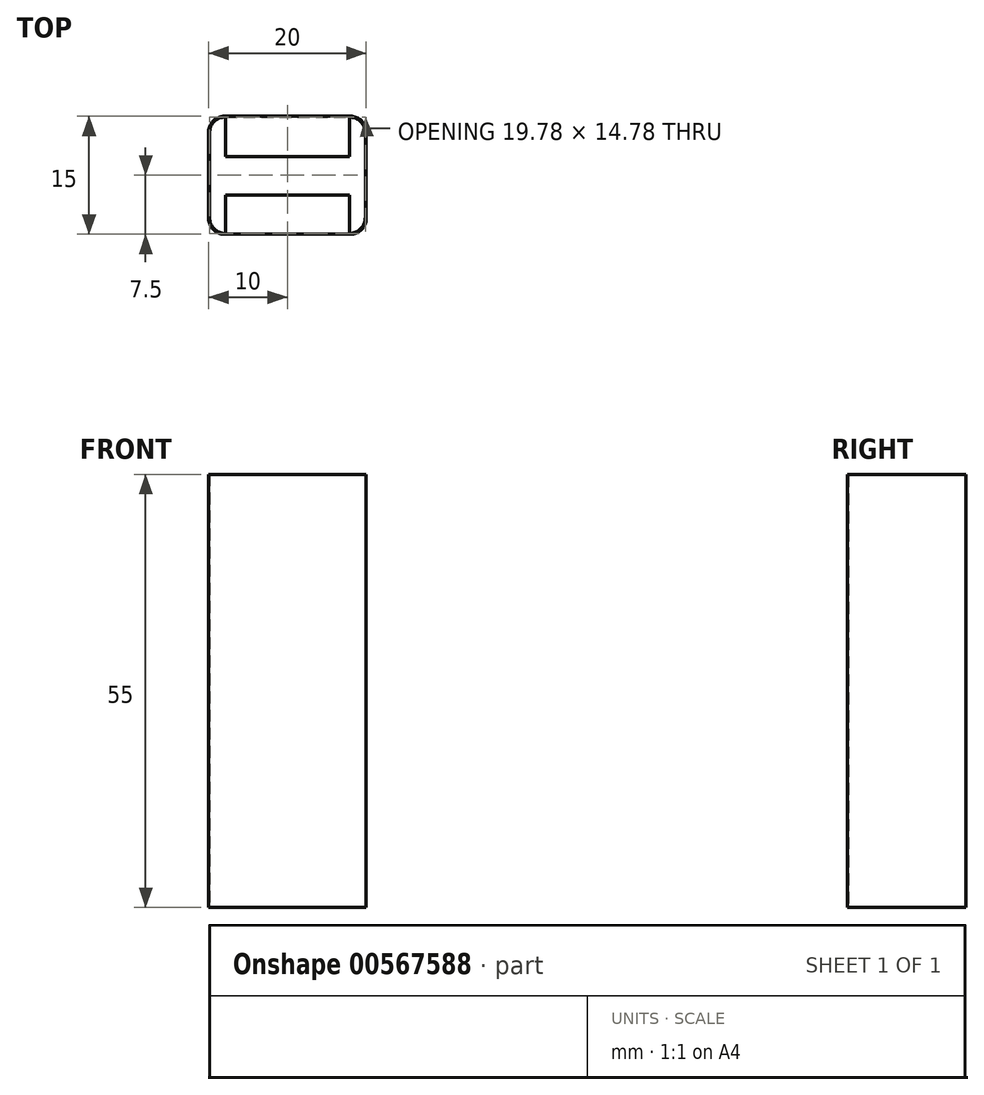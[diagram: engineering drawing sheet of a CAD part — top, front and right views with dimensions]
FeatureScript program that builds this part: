
annotation { "Feature Type Name" : "Feature", "Feature Type Description" : "" }
export const myFeature = defineFeature(function(context is Context, id is Id, definition is map)
    precondition{}
    {
        {
            var Q0;
            Q0=qCreatedBy(makeId("Top.planeOp"),FACE);
            var sketch = newSketch(context, id + "F0", { "sketchPlane" : qUnion([Q0])});
            skLineSegment(sketch, "E0.bottom", {"start": v(8, -7.5) * mm, "end": v(-8, -7.5) * mm});
            skLineSegment(sketch, "E0.top", {"start": v(8, 7.5) * mm, "end": v(-8, 7.5) * mm});
            skLineSegment(sketch, "E0.left", {"start": v(10, -5.5) * mm, "end": v(10, 5.5) * mm});
            skLineSegment(sketch, "E0.right", {"start": v(-10, -5.5) * mm, "end": v(-10, 5.5) * mm});
            skPoint(sketch, "E0.middle", {"position": v(0, 0) * mm});
            skPoint(sketch, "E1.visualSharp", {"position": v(-10, 7.5) * mm});
            skArc(sketch, "E1.filletArc", {"start": v(-8, 7.5) * mm, "mid": v(-9.41, 6.91) * mm, "end": v(-10, 5.5) * mm});
            skPoint(sketch, "E2.visualSharp", {"position": v(10, 7.5) * mm});
            skArc(sketch, "E2.filletArc", {"start": v(10, 5.5) * mm, "mid": v(9.41, 6.91) * mm, "end": v(8, 7.5) * mm});
            skPoint(sketch, "E3.visualSharp", {"position": v(10, -7.5) * mm});
            skArc(sketch, "E3.filletArc", {"start": v(8, -7.5) * mm, "mid": v(9.41, -6.91) * mm, "end": v(10, -5.5) * mm});
            skPoint(sketch, "E4.visualSharp", {"position": v(-10, -7.5) * mm});
            skArc(sketch, "E4.filletArc", {"start": v(-10, -5.5) * mm, "mid": v(-9.41, -6.91) * mm, "end": v(-8, -7.5) * mm});
            skLineSegment(sketch, "E5.0", {"start": v(7.9, 7.4) * mm, "end": v(-7.9, 7.39) * mm});
            skLineSegment(sketch, "E5.1", {"start": v(9.9, -5.4) * mm, "end": v(9.9, 5.4) * mm});
            skLineSegment(sketch, "E5.2", {"start": v(7.9, -7.39) * mm, "end": v(-7.89, -7.4) * mm});
            skLineSegment(sketch, "E5.3", {"start": v(-9.89, -5.4) * mm, "end": v(-9.89, 5.39) * mm});
            skPoint(sketch, "E6.visualSharp", {"position": v(-9.9, 7.39) * mm});
            skArc(sketch, "E6.filletArc", {"start": v(-7.9, 7.39) * mm, "mid": v(-9.3, 6.8) * mm, "end": v(-9.89, 5.39) * mm});
            skPoint(sketch, "E7.visualSharp", {"position": v(-9.89, -7.4) * mm});
            skArc(sketch, "E7.filletArc", {"start": v(-9.89, -5.4) * mm, "mid": v(-9.3, -6.8) * mm, "end": v(-7.89, -7.39) * mm});
            skPoint(sketch, "E8.visualSharp", {"position": v(9.9, -7.39) * mm});
            skArc(sketch, "E8.filletArc", {"start": v(7.9, -7.39) * mm, "mid": v(9.3, -6.8) * mm, "end": v(9.9, -5.4) * mm});
            skPoint(sketch, "E9.visualSharp", {"position": v(9.89, 7.4) * mm});
            skArc(sketch, "E9.filletArc", {"start": v(9.89, 5.4) * mm, "mid": v(9.3, 6.8) * mm, "end": v(7.9, 7.4) * mm});
            skSolve(sketch);
        }
        {
            var Q0;
            Q0=makeQuery(id+"F0.imprint","IMPRINT",FACE,{"disambiguationData":[TD([[makeQuery(id+"F0.imprint","IMPRINT",EDGE,{"derivedFrom":sQuery(id+"F0.wireOp",EDGE,"E0.bottom")}),-1.0]])]});
            extrude(context, id + "F1", {"entities" : qUnion([Q0]), "depth" : 30 * mm, "offsetDistance" : 25 * mm});
        }
        {
            var Q0;
            Q0=makeQuery(id+"F1.opExtrude","SWEPT_FACE",FACE,{"disambiguationData":[OSD([sQuery(id+"F0.wireOp",EDGE,"E5.0")])]});
            var sketch = newSketch(context, id + "F2", { "sketchPlane" : qUnion([Q0])});
            skLineSegment(sketch, "E10.bottom", {"start": v(-7.89, 30) * mm, "end": v(7.9, 30) * mm});
            skLineSegment(sketch, "E10.top", {"start": v(-7.89, 29.89) * mm, "end": v(7.9, 29.89) * mm});
            skLineSegment(sketch, "E10.left", {"start": v(-7.89, 30) * mm, "end": v(-7.89, 29.89) * mm});
            skLineSegment(sketch, "E10.right", {"start": v(7.9, 30) * mm, "end": v(7.9, 29.89) * mm});
            skSolve(sketch);
        }
        {
            var Q0;
            Q0=makeQuery(id+"F2.imprint","IMPRINT",FACE,{"disambiguationData":[TD([[makeQuery(id+"F2.imprint","IMPRINT",EDGE,{"derivedFrom":sQuery(id+"F2.wireOp",EDGE,"E10.bottom")}),1.0]])]});
            extrude(context, id + "F3", {"entities" : qUnion([Q0]), "operationType" : NewBodyOperationType.ADD, "depth" : 5 * mm, "offsetDistance" : 25 * mm});
        }
        {
            var Q0;
            Q0=makeQuery(id+"F1.opExtrude","SWEPT_FACE",FACE,{"disambiguationData":[OSD([sQuery(id+"F0.wireOp",EDGE,"E5.2")])]});
            var sketch = newSketch(context, id + "F4", { "sketchPlane" : qUnion([Q0])});
            skLineSegment(sketch, "E11.bottom", {"start": v(-7.9, 30) * mm, "end": v(7.89, 30) * mm});
            skLineSegment(sketch, "E11.top", {"start": v(-7.9, 29.9) * mm, "end": v(7.89, 29.9) * mm});
            skLineSegment(sketch, "E11.left", {"start": v(-7.9, 30) * mm, "end": v(-7.9, 29.9) * mm});
            skLineSegment(sketch, "E11.right", {"start": v(7.89, 30) * mm, "end": v(7.89, 29.9) * mm});
            skSolve(sketch);
        }
        {
            var Q0;
            Q0=makeQuery(id+"F4.imprint","IMPRINT",FACE,{"disambiguationData":[TD([[makeQuery(id+"F4.imprint","IMPRINT",EDGE,{"derivedFrom":sQuery(id+"F4.wireOp",EDGE,"E11.bottom")}),-1.0]])]});
            extrude(context, id + "F5", {"entities" : qUnion([Q0]), "operationType" : NewBodyOperationType.ADD, "depth" : 4.9 * mm, "offsetDistance" : 25 * mm});
        }
        {
            var Q0;
            Q0=makeQuery(id+"F1.opExtrude","CAP_FACE",FACE,{"disambiguationData":[OSD([sQuery(id+"F0.wireOp",EDGE,"E0.bottom"),sQuery(id+"F0.wireOp",EDGE,"E0.top"),sQuery(id+"F0.wireOp",EDGE,"E0.left"),sQuery(id+"F0.wireOp",EDGE,"E0.right"),sQuery(id+"F0.wireOp",EDGE,"E1.filletArc"),sQuery(id+"F0.wireOp",EDGE,"E2.filletArc"),sQuery(id+"F0.wireOp",EDGE,"E3.filletArc"),sQuery(id+"F0.wireOp",EDGE,"E4.filletArc"),sQuery(id+"F0.wireOp",EDGE,"E5.0"),sQuery(id+"F0.wireOp",EDGE,"E5.1"),sQuery(id+"F0.wireOp",EDGE,"E5.2"),sQuery(id+"F0.wireOp",EDGE,"E5.3"),sQuery(id+"F0.wireOp",EDGE,"E6.filletArc"),sQuery(id+"F0.wireOp",EDGE,"E7.filletArc"),sQuery(id+"F0.wireOp",EDGE,"E8.filletArc"),sQuery(id+"F0.wireOp",EDGE,"E9.filletArc")])],"isStart":true});
            extrude(context, id + "F6", {"entities" : qUnion([Q0]), "operationType" : NewBodyOperationType.ADD, "depth" : 25 * mm, "offsetDistance" : 25 * mm});
        }
    });
